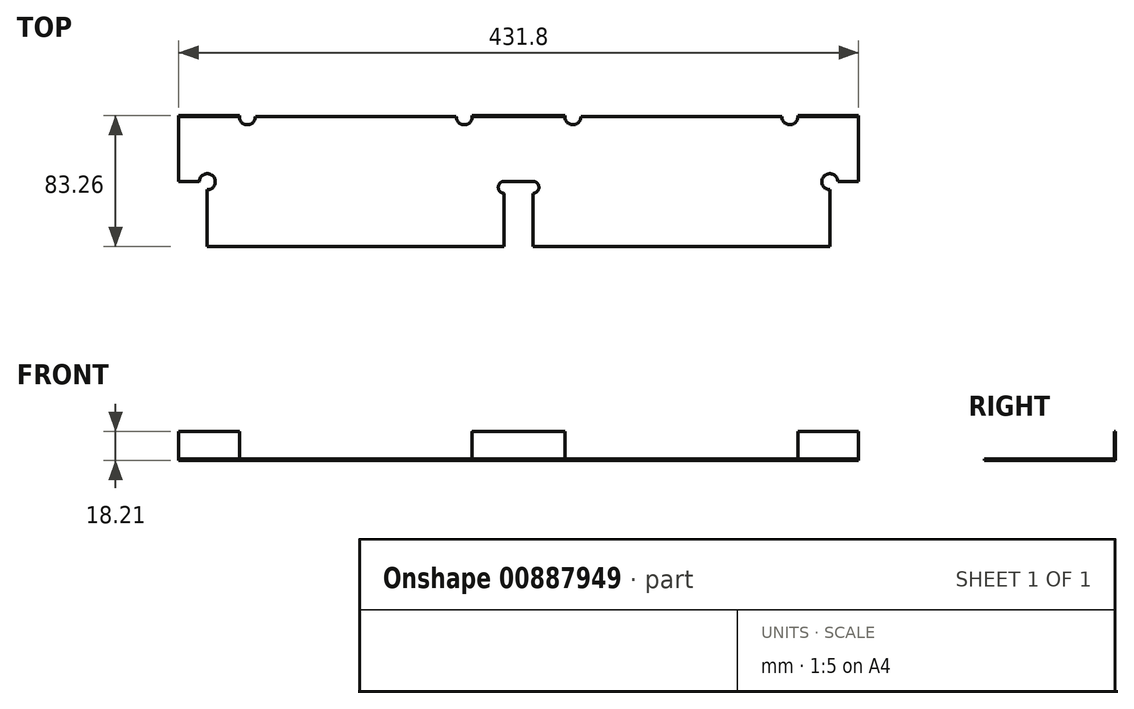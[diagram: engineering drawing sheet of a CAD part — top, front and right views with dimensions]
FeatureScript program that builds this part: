
annotation { "Feature Type Name" : "Feature", "Feature Type Description" : "" }
export const myFeature = defineFeature(function(context is Context, id is Id, definition is map)
    precondition{}
    {
        {
            assignVariable(context, id + "F0", {"name" : "WoodThickness", "anyValue" : .717});
        }
        {
            var Q0;
            Q0=qCreatedBy(makeId("Top.planeOp"),FACE);
            var sketch = newSketch(context, id + "F1", { "sketchPlane" : qUnion([Q0])});
            skLineSegment(sketch, "E0.bottom", {"start": v(215.9, 41.28) * mm, "end": v(-215.9, 41.28) * mm});
            skLineSegment(sketch, "E0.top", {"start": v(215.9, -41.27) * mm, "end": v(-215.9, -41.27) * mm});
            skLineSegment(sketch, "E0.left", {"start": v(215.9, 41.28) * mm, "end": v(215.9, -41.28) * mm});
            skLineSegment(sketch, "E0.right", {"start": v(-215.9, 41.28) * mm, "end": v(-215.9, -41.28) * mm});
            skPoint(sketch, "E0.middle", {"position": v(0, 0) * mm});
            skSolve(sketch);
        }
        {
            var Q0;
            Q0=qSketchRegion(id+"F1",true);
            extrude(context, id + "F2", {"entities" : qUnion([Q0]), "depth" : (getVariable(context, 'WoodThickness')) * mm, "offsetDistance" : 25.4 * mm});
        }
        {
            var Q0;
            Q0=makeQuery(id+"F2.opExtrude","CAP_FACE",FACE,{"disambiguationData":[OSD([sQuery(id+"F1.wireOp",EDGE,"E0.bottom"),sQuery(id+"F1.wireOp",EDGE,"E0.top"),sQuery(id+"F1.wireOp",EDGE,"E0.left"),sQuery(id+"F1.wireOp",EDGE,"E0.right")])],"isStart":false});
            var sketch = newSketch(context, id + "F3", { "sketchPlane" : qUnion([Q0])});
            skLineSegment(sketch, "E1.bottom", {"start": v(-215.9, -41.27) * mm, "end": v(-197.69, -41.27) * mm});
            skLineSegment(sketch, "E1.top", {"start": v(-215.9, 0) * mm, "end": v(-197.69, 0) * mm});
            skLineSegment(sketch, "E1.left", {"start": v(-215.9, -41.28) * mm, "end": v(-215.9, 0) * mm});
            skLineSegment(sketch, "E1.right", {"start": v(-197.69, -41.27) * mm, "end": v(-197.69, 0) * mm});
            skLineSegment(sketch, "E2", {"start": v(0, 41.28) * mm, "end": v(0, -41.27) * mm, "construction": true});
            skArc(sketch, "E3", {"start": v(-197.69, -5.08) * mm, "mid": v(-194.1, 3.6) * mm, "end": v(-202.77, 0) * mm});
            skLineSegment(sketch, "E4.MirrorCS", {"start": v(215.9, 0) * mm, "end": v(197.69, 0) * mm});
            skLineSegment(sketch, "E5.MirrorCS", {"start": v(197.69, -41.28) * mm, "end": v(197.69, 0) * mm});
            skArc(sketch, "E6.MirrorCS", {"start": v(197.69, -5.08) * mm, "mid": v(194.1, 3.6) * mm, "end": v(202.77, 0) * mm});
            skSolve(sketch);
        }
        {
            var Q0;
            Q0=qSketchRegion(id+"F3",true);
            var Q1;
            {var subQ6=sQuery(id+"F3.wireOp",EDGE,"7f1c7eb7-cb9b-46c9-a52e-6439d7ca592f0.MirrorCS");Q1=makeQuery(id+"F3.imprint","IMPRINT",FACE,{"disambiguationData":[TD([[makeQuery(id+"F3.imprint","IMPRINT",EDGE,{"derivedFrom":subQ6}),1.0]])]});}
            var Q2;
            {var subQ1=sQuery(id+"F3.wireOp",EDGE,"E4.MirrorCS");var subQ8=makeQuery(id+"F2.opExtrude","CAP_EDGE",EDGE,{"disambiguationData":[OSD([sQuery(id+"F1.wireOp",EDGE,"E0.left")])],"isStart":false});var subQ9=makeQuery(id+"F3.imprint","INTERSECT",VERTEX,{"derivedFrom":[subQ8,subQ1]});Q2=makeQuery(id+"F3.imprint","IMPRINT",FACE,{"disambiguationData":[TD([[makeQuery(id+"F3.imprint","IMPRINT",EDGE,{"disambiguationData":[TD([[subQ9,-1.0]])],"derivedFrom":subQ1}),1.0]])]});}
            extrude(context, id + "F4", {"entities" : qUnion([Q0, Q1, Q2]), "operationType" : NewBodyOperationType.REMOVE, "endBound" : BoundingType.THROUGH_ALL, "oppositeDirection" : true, "depth" : 25.4 * mm, "offsetDistance" : 25.4 * mm});
        }
        {
            var Q0;
            Q0=makeQuery(id+"F2.opExtrude","CAP_FACE",FACE,{"disambiguationData":[OSD([sQuery(id+"F1.wireOp",EDGE,"E0.bottom"),sQuery(id+"F1.wireOp",EDGE,"E0.top"),sQuery(id+"F1.wireOp",EDGE,"E0.left"),sQuery(id+"F1.wireOp",EDGE,"E0.right")])],"isStart":false});
            var sketch = newSketch(context, id + "F5", { "sketchPlane" : qUnion([Q0])});
            skLineSegment(sketch, "E7.bottom", {"start": v(-9.1, -41.27) * mm, "end": v(9.1, -41.27) * mm});
            skLineSegment(sketch, "E7.top", {"start": v(-9.1, 0) * mm, "end": v(9.1, 0) * mm});
            skLineSegment(sketch, "E7.left", {"start": v(-9.1, -41.27) * mm, "end": v(-9.1, 0) * mm});
            skLineSegment(sketch, "E7.right", {"start": v(9.1, -41.27) * mm, "end": v(9.1, 0) * mm});
            skArc(sketch, "E8", {"start": v(-9.1, -7.4) * mm, "mid": v(-12.86, -2.95) * mm, "end": v(-7.84, 0) * mm});
            skArc(sketch, "E9", {"start": v(9.1, -7.4) * mm, "mid": v(12.86, -2.95) * mm, "end": v(7.84, 0) * mm});
            skLineSegment(sketch, "E10", {"start": v(-9.1, 0) * mm, "end": v(0, 0) * mm, "construction": true});
            skLineSegment(sketch, "E11", {"start": v(0, 0) * mm, "end": v(9.1, 0) * mm, "construction": true});
            skLineSegment(sketch, "E12", {"start": v(0, 41.28) * mm, "end": v(0, -41.27) * mm, "construction": true});
            skSolve(sketch);
        }
        {
            var Q0;
            Q0 = qSketchRegion(id + "F5", true);
            extrude(context, id + "F6", {"entities" : qUnion([Q0]), "operationType" : NewBodyOperationType.REMOVE, "endBound" : BoundingType.THROUGH_ALL, "oppositeDirection" : true, "depth" : 25.4 * mm, "offsetDistance" : 25.4 * mm});
        }
        {
            var Q0;
            Q0=makeQuery(id+"F2.opExtrude","SWEPT_FACE",FACE,{"disambiguationData":[OSD([sQuery(id+"F1.wireOp",EDGE,"E0.bottom")])]});
            var sketch = newSketch(context, id + "F7", { "sketchPlane" : qUnion([Q0])});
            skLineSegment(sketch, "E13.bottom", {"start": v(-9.1, 18.21) * mm, "end": v(9.1, 18.21) * mm});
            skLineSegment(sketch, "E13.top", {"start": v(-9.1, 0) * mm, "end": v(9.1, 0) * mm});
            skLineSegment(sketch, "E13.left", {"start": v(-9.1, 18.21) * mm, "end": v(-9.1, 0) * mm});
            skLineSegment(sketch, "E13.right", {"start": v(9.1, 18.21) * mm, "end": v(9.1, 0) * mm});
            skLineSegment(sketch, "E14", {"start": v(0, 0) * mm, "end": v(0, 18.21) * mm, "construction": true});
            skLineSegment(sketch, "E15.bottom", {"start": v(9.1, 18.21) * mm, "end": v(34.5, 18.21) * mm});
            skLineSegment(sketch, "E15.top", {"start": v(9.1, 0) * mm, "end": v(34.5, 0) * mm});
            skLineSegment(sketch, "E15.right", {"start": v(34.5, 18.21) * mm, "end": v(34.5, 0) * mm});
            skLineSegment(sketch, "E16.bottom", {"start": v(-9.1, 18.21) * mm, "end": v(-34.5, 18.21) * mm});
            skLineSegment(sketch, "E16.top", {"start": v(-9.1, 0) * mm, "end": v(-34.5, 0) * mm});
            skLineSegment(sketch, "E16.right", {"start": v(-34.5, 18.21) * mm, "end": v(-34.5, 0) * mm});
            skLineSegment(sketch, "E17.bottom", {"start": v(-215.9, 18.21) * mm, "end": v(-197.69, 18.21) * mm});
            skLineSegment(sketch, "E17.top", {"start": v(-215.9, 0) * mm, "end": v(-197.69, 0) * mm});
            skLineSegment(sketch, "E17.left", {"start": v(-215.9, 18.21) * mm, "end": v(-215.9, 0) * mm});
            skLineSegment(sketch, "E17.right", {"start": v(-197.69, 18.21) * mm, "end": v(-197.69, 0) * mm});
            skLineSegment(sketch, "E18.bottom", {"start": v(-197.69, 18.21) * mm, "end": v(-172.29, 18.21) * mm});
            skLineSegment(sketch, "E18.top", {"start": v(-197.69, 0) * mm, "end": v(-172.29, 0) * mm});
            skLineSegment(sketch, "E18.right", {"start": v(-172.29, 18.21) * mm, "end": v(-172.29, 0) * mm});
            skLineSegment(sketch, "E19.MirrorCS", {"start": v(172.29, 18.21) * mm, "end": v(172.29, 0) * mm});
            skLineSegment(sketch, "E20.MirrorCS", {"start": v(197.69, 18.21) * mm, "end": v(172.29, 18.21) * mm});
            skLineSegment(sketch, "E21.MirrorCS", {"start": v(197.69, 18.21) * mm, "end": v(197.69, 0) * mm});
            skLineSegment(sketch, "E22.MirrorCS", {"start": v(197.69, 0) * mm, "end": v(172.29, 0) * mm});
            skLineSegment(sketch, "E23.MirrorCS", {"start": v(215.9, 0) * mm, "end": v(197.69, 0) * mm});
            skLineSegment(sketch, "E24.MirrorCS", {"start": v(215.9, 18.21) * mm, "end": v(215.9, 0) * mm});
            skLineSegment(sketch, "E25.MirrorCS", {"start": v(215.9, 18.21) * mm, "end": v(197.69, 18.21) * mm});
            skSolve(sketch);
        }
        {
            var Q0;
            Q0 = qSketchRegion(id + "F7", true);
            extrude(context, id + "F8", {"entities" : qUnion([Q0]), "operationType" : NewBodyOperationType.ADD, "depth" : (getVariable(context, 'WoodThickness')) * mm, "offsetDistance" : 25.4 * mm});
        }
        {
            var Q0;
            Q0=makeQuery(id+"F8.boolean.opBoolean","MERGE",FACE,{"derivedFrom":[makeQuery(id+"F2.opExtrude","CAP_FACE",FACE,{"disambiguationData":[OSD([sQuery(id+"F1.wireOp",EDGE,"E0.bottom"),sQuery(id+"F1.wireOp",EDGE,"E0.top"),sQuery(id+"F1.wireOp",EDGE,"E0.left"),sQuery(id+"F1.wireOp",EDGE,"E0.right")])],"isStart":true}),makeQuery(id+"F8.opExtrude","SWEPT_FACE",FACE,{"disambiguationData":[OSD([sQuery(id+"F7.wireOp",EDGE,"E13.top"),sQuery(id+"F7.wireOp",EDGE,"E15.top"),sQuery(id+"F7.wireOp",EDGE,"E16.top")])]})]});
            var sketch = newSketch(context, id + "F9", { "sketchPlane" : qUnion([Q0])});
            skCircle(sketch, "E26", {"center": v(34.5, -41.28) * mm, "radius": 5.08 * mm});
            skCircle(sketch, "E27", {"center": v(-34.5, -41.28) * mm, "radius": 5.08 * mm});
            skCircle(sketch, "E28", {"center": v(172.29, -41.28) * mm, "radius": 5.08 * mm});
            skCircle(sketch, "E29", {"center": v(-172.29, -41.28) * mm, "radius": 5.08 * mm});
            skSolve(sketch);
        }
        {
            var Q0;
            Q0 = qSketchRegion(id + "F9", true);
            extrude(context, id + "F10", {"entities" : qUnion([Q0]), "operationType" : NewBodyOperationType.REMOVE, "endBound" : BoundingType.THROUGH_ALL, "oppositeDirection" : true, "depth" : 25.4 * mm, "offsetDistance" : 25.4 * mm});
        }
    });
